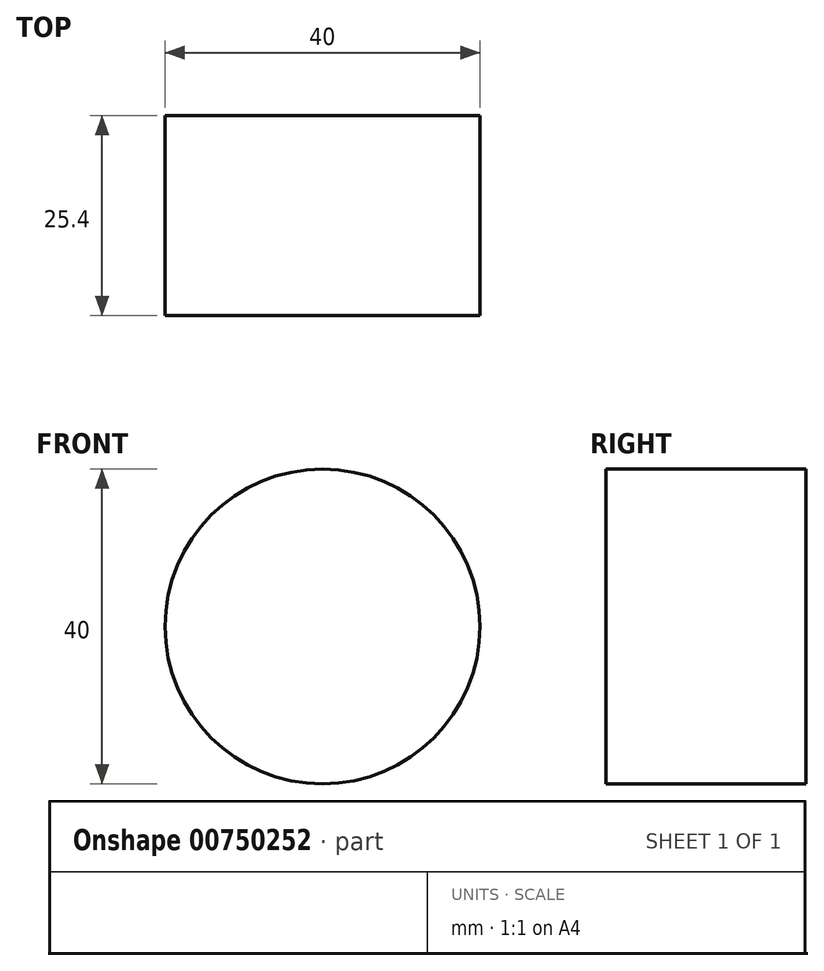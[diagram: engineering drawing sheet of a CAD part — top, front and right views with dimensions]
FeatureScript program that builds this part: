
annotation { "Feature Type Name" : "Feature", "Feature Type Description" : "" }
export const myFeature = defineFeature(function(context is Context, id is Id, definition is map)
    precondition{}
    {
        {
            var Q0;
            Q0=qCreatedBy(makeId("Front.planeOp"),FACE);
            var sketch = newSketch(context, id + "F0", { "sketchPlane" : qUnion([Q0])});
            skCircle(sketch, "E0", {"center": v(-86.92, 18.03) * mm, "radius": 20 * mm});
            skSolve(sketch);
        }
        {
            var Q0;
            Q0 = qSketchRegion(id + "F0", true);
            extrude(context, id + "F1", {"entities" : qUnion([Q0]), "depth" : 25.4 * mm, "offsetDistance" : 25.4 * mm});
        }
    });
